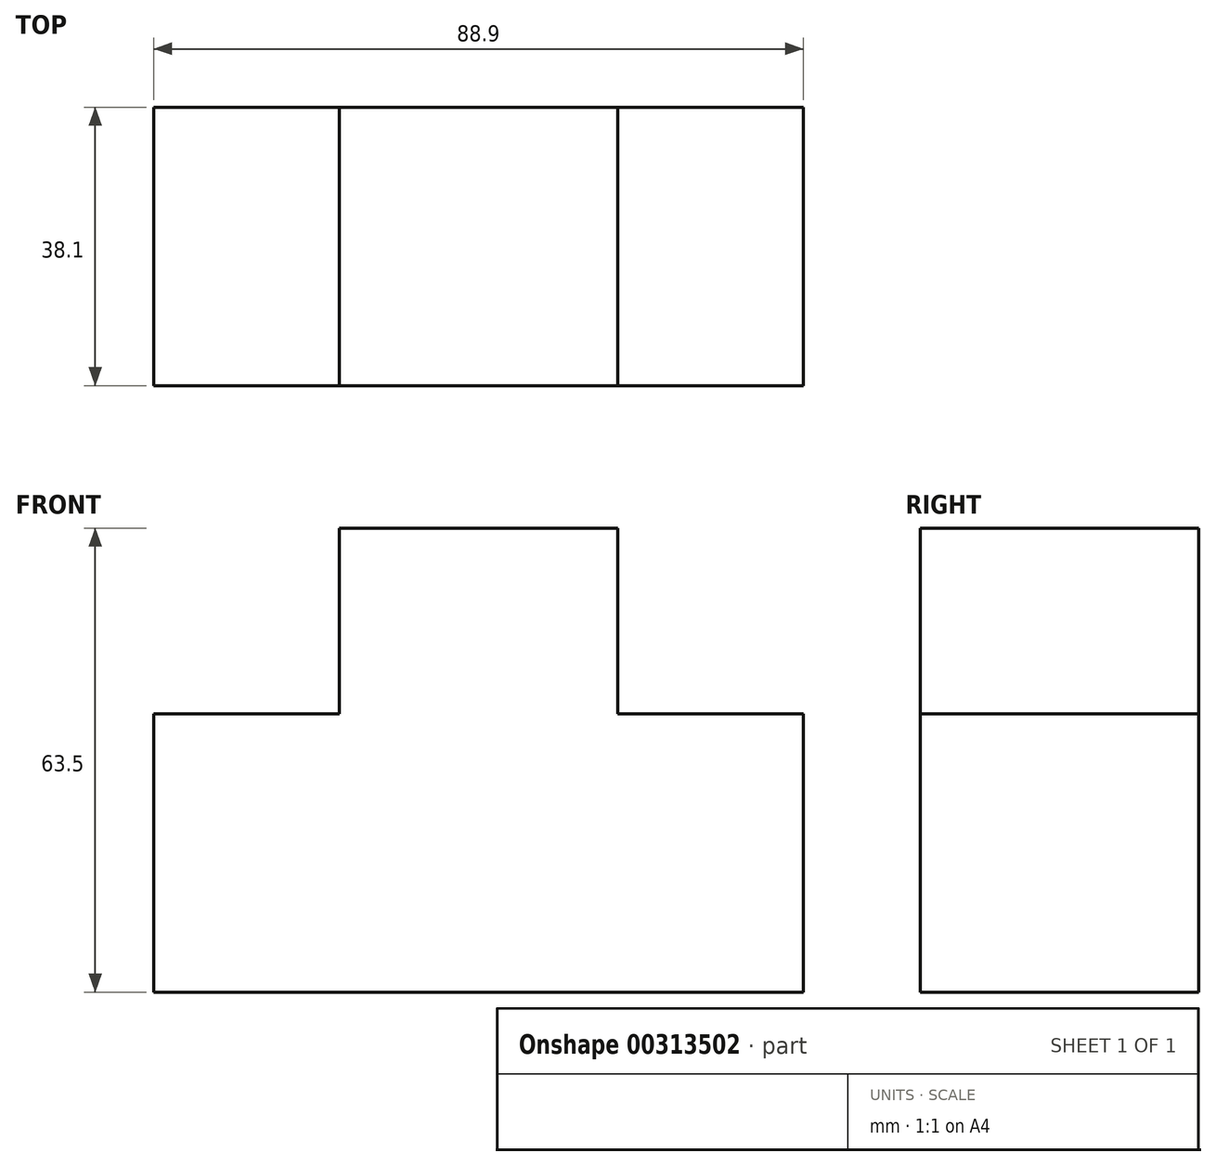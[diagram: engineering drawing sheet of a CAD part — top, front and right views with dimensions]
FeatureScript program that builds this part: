
annotation { "Feature Type Name" : "Feature", "Feature Type Description" : "" }
export const myFeature = defineFeature(function(context is Context, id is Id, definition is map)
    precondition{}
    {
        {
            var Q0;
            Q0=qCreatedBy(makeId("Front.planeOp"),FACE);
            var sketch = newSketch(context, id + "F0", { "sketchPlane" : qUnion([Q0])});
            skLineSegment(sketch, "E0", {"start": v(-46.39, -48.43) * mm, "end": v(42.51, -48.43) * mm});
            skLineSegment(sketch, "E1", {"start": v(42.51, -48.43) * mm, "end": v(42.51, -10.33) * mm});
            skLineSegment(sketch, "E2", {"start": v(42.51, -10.33) * mm, "end": v(17.11, -10.33) * mm});
            skLineSegment(sketch, "E3", {"start": v(17.11, 15.07) * mm, "end": v(-20.99, 15.07) * mm});
            skLineSegment(sketch, "E4", {"start": v(-20.99, 15.07) * mm, "end": v(-20.99, -10.33) * mm});
            skLineSegment(sketch, "E5", {"start": v(17.11, 15.07) * mm, "end": v(17.11, -10.33) * mm});
            skLineSegment(sketch, "E6", {"start": v(-20.99, -10.33) * mm, "end": v(-46.39, -10.33) * mm});
            skLineSegment(sketch, "E7", {"start": v(-46.39, -10.33) * mm, "end": v(-46.39, -48.43) * mm});
            skSolve(sketch);
        }
        {
            var Q0;
            Q0 = qSketchRegion(id + "F0", true);
            extrude(context, id + "F1", {"entities" : qUnion([Q0]), "depth" : 38.1 * mm});
        }
    });
